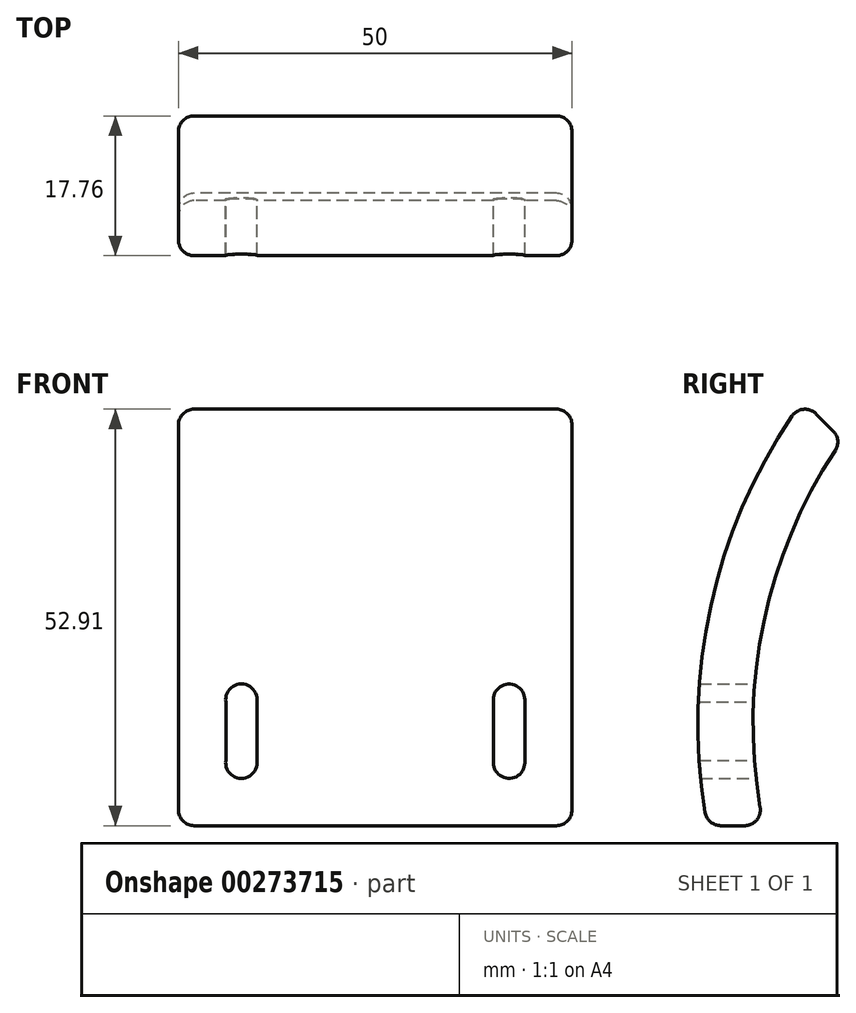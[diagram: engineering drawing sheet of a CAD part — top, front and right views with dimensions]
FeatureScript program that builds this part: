
annotation { "Feature Type Name" : "Feature", "Feature Type Description" : "" }
export const myFeature = defineFeature(function(context is Context, id is Id, definition is map)
    precondition{}
    {
        {
            var Q0;
            Q0=qCreatedBy(makeId("Right.planeOp"),FACE);
            var sketch = newSketch(context, id + "F0", { "sketchPlane" : qUnion([Q0])});
            skArc(sketch, "E0", {"start": v(-20, 14.2) * mm, "mid": v(-20.07, 39.74) * mm, "end": v(-10, 63.2) * mm});
            skArc(sketch, "E1.0", {"start": v(-27.14, 14.2) * mm, "mid": v(-26.64, 42.46) * mm, "end": v(-15.02, 68.22) * mm});
            skLineSegment(sketch, "E2", {"start": v(-15.02, 68.22) * mm, "end": v(-10, 63.2) * mm});
            skLineSegment(sketch, "E3", {"start": v(-27.14, 14.2) * mm, "end": v(-20, 14.2) * mm});
            skSolve(sketch);
        }
        {
            var Q0;
            Q0 = qSketchRegion(id + "F0", true);
            extrude(context, id + "F1", {"entities" : qUnion([Q0]), "depth" : 50 * mm});
        }
        {
            var Q0;
            Q0=qCreatedBy(makeId("Front.planeOp"),FACE);
            var sketch = newSketch(context, id + "F2", { "sketchPlane" : qUnion([Q0])});
            skCircle(sketch, "E4", {"center": v(8, 22.2) * mm, "radius": 2 * mm});
            skCircle(sketch, "E5", {"center": v(8, 30.2) * mm, "radius": 2 * mm});
            skCircle(sketch, "E6", {"center": v(42, 22.2) * mm, "radius": 2 * mm});
            skCircle(sketch, "E7", {"center": v(42, 30.2) * mm, "radius": 2 * mm});
            skLineSegment(sketch, "E8", {"start": v(6.02, 29.91) * mm, "end": v(6.02, 21.91) * mm});
            skLineSegment(sketch, "E9", {"start": v(10, 30.2) * mm, "end": v(10, 22.2) * mm});
            skLineSegment(sketch, "E10", {"start": v(40, 30.2) * mm, "end": v(40, 22.2) * mm});
            skLineSegment(sketch, "E11", {"start": v(44, 30.2) * mm, "end": v(44, 22.2) * mm});
            skSolve(sketch);
        }
        {
            var Q0;
            Q0 = qSketchRegion(id + "F2", true);
            extrude(context, id + "F3", {"entities" : qUnion([Q0]), "operationType" : NewBodyOperationType.REMOVE, "depth" : 50 * mm});
        }
        {
            var Q0;
            Q0=makeQuery(id+"F1.opExtrude","CAP_FACE",FACE,{"disambiguationData":[OSD([sQuery(id+"F0.wireOp",EDGE,"E0"),sQuery(id+"F0.wireOp",EDGE,"E1.0"),sQuery(id+"F0.wireOp",EDGE,"E2"),sQuery(id+"F0.wireOp",EDGE,"E3")])],"isStart":false});
            var Q1;
            Q1=makeQuery(id+"F1.opExtrude","SWEPT_FACE",FACE,{"disambiguationData":[OSD([sQuery(id+"F0.wireOp",EDGE,"E2")])]});
            var Q2;
            Q2=makeQuery(id+"F1.opExtrude","CAP_FACE",FACE,{"disambiguationData":[OSD([sQuery(id+"F0.wireOp",EDGE,"E0"),sQuery(id+"F0.wireOp",EDGE,"E1.0"),sQuery(id+"F0.wireOp",EDGE,"E2"),sQuery(id+"F0.wireOp",EDGE,"E3")])],"isStart":true});
            var Q3;
            Q3=makeQuery(id+"F1.opExtrude","SWEPT_FACE",FACE,{"disambiguationData":[OSD([sQuery(id+"F0.wireOp",EDGE,"E3")])]});
            fillet(context, id + "F4", {"entities" : qUnion([Q0, Q1, Q2, Q3]), "radius" : 2 * mm, "allowEdgeOverflow" : false});
        }
    });
